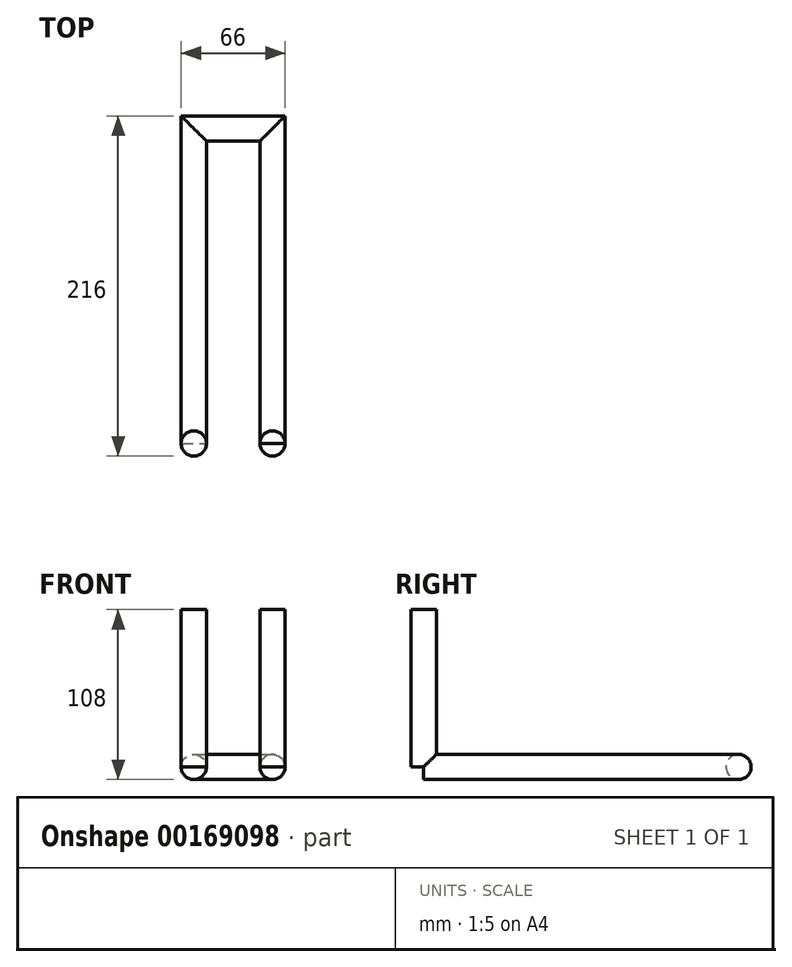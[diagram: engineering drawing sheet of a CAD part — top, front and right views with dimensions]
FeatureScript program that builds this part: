
annotation { "Feature Type Name" : "Feature", "Feature Type Description" : "" }
export const myFeature = defineFeature(function(context is Context, id is Id, definition is map)
    precondition{}
    {
        {
            var Q0;
            Q0=qCreatedBy(makeId("Top.planeOp"),FACE);
            var sketch = newSketch(context, id + "F0", { "sketchPlane" : qUnion([Q0])});
            skLineSegment(sketch, "E0", {"start": v(0, 0) * mm, "end": v(0, 84.53) * mm, "construction": true});
            skLineSegment(sketch, "E1", {"start": v(-25, 0) * mm, "end": v(-25, 200) * mm});
            skLineSegment(sketch, "E2", {"start": v(-25, 200) * mm, "end": v(0, 200) * mm});
            skLineSegment(sketch, "E3.MirrorCS", {"start": v(25, 200) * mm, "end": v(0, 200) * mm});
            skLineSegment(sketch, "E4.MirrorCS", {"start": v(25, 0) * mm, "end": v(25, 200) * mm});
            skSolve(sketch);
        }
        {
            var Q0;
            Q0=qCreatedBy(makeId("Top.planeOp"),FACE);
            var sketch = newSketch(context, id + "F1", { "sketchPlane" : qUnion([Q0])});
            skCircle(sketch, "E5", {"center": v(-25, 0) * mm, "radius": 8 * mm});
            skCircle(sketch, "E6", {"center": v(25, 0) * mm, "radius": 8 * mm});
            skSolve(sketch);
        }
        {
            var Q0;
            Q0=qCreatedBy(makeId("Front.planeOp"),FACE);
            var sketch = newSketch(context, id + "F2", { "sketchPlane" : qUnion([Q0])});
            skCircle(sketch, "E7", {"center": v(-25, 0) * mm, "radius": 8 * mm});
            skSolve(sketch);
        }
        {
            var Q0;
            Q0 = qSketchRegion(id + "F1", true);
            extrude(context, id + "F3", {"entities" : qUnion([Q0]), "depth" : 100 * mm});
        }
        {
            var Q0;
            Q0 = qSketchRegion(id + "F2", true);
            var Q1;
            Q1 = qConstructionFilter(qBodyType(qCreatedBy(id + "F0" ,EDGE), BodyType.WIRE), ConstructionObject.NO);
            sweep(context, id + "F4", {"operationType" : NewBodyOperationType.ADD, "profiles" : qUnion([Q0]), "path" : qUnion([Q1])});
        }
    });
